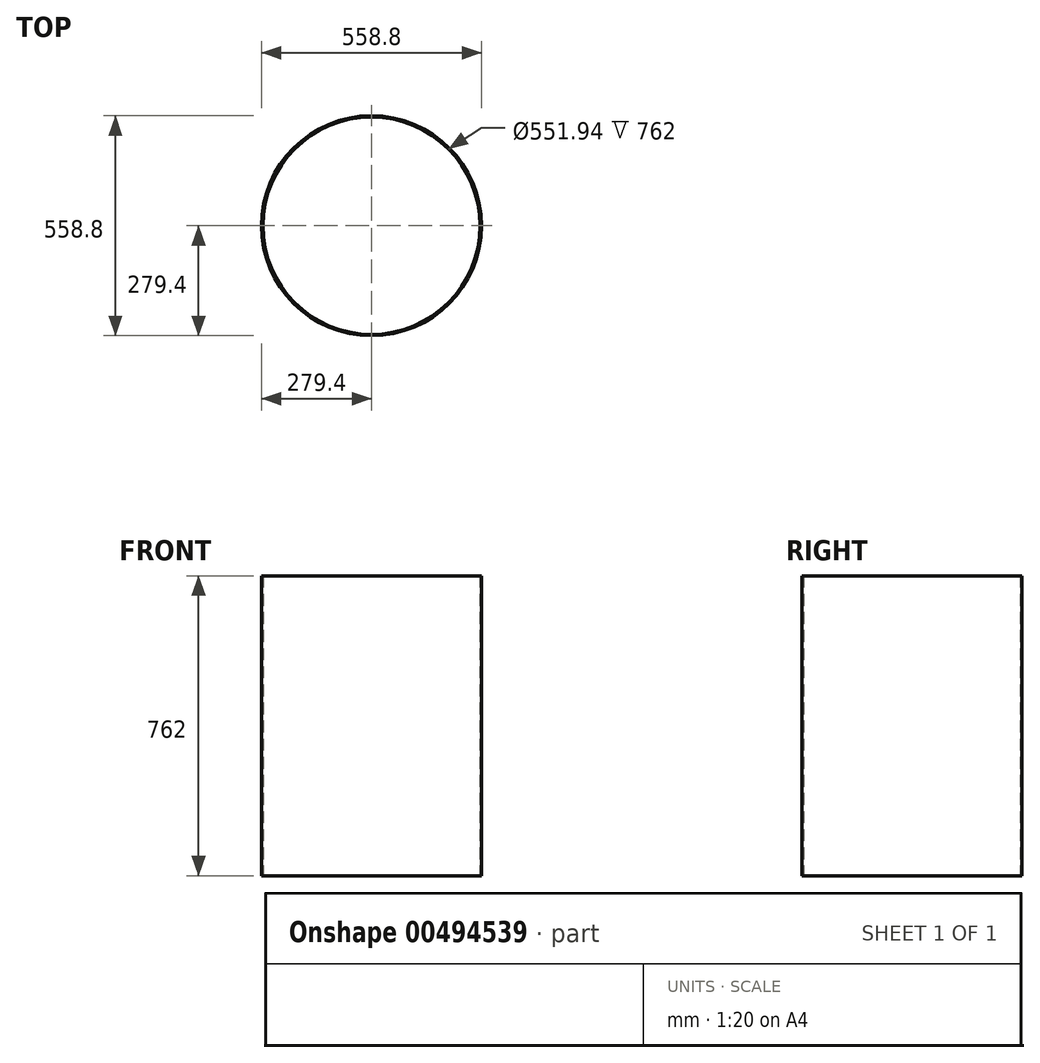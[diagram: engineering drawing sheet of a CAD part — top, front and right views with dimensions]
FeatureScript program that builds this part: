
annotation { "Feature Type Name" : "Feature", "Feature Type Description" : "" }
export const myFeature = defineFeature(function(context is Context, id is Id, definition is map)
    precondition{}
    {
        {
            var Q0;
            Q0=qCreatedBy(makeId("Top.planeOp"),FACE);
            var sketch = newSketch(context, id + "F0", { "sketchPlane" : qUnion([Q0])});
            skCircle(sketch, "E0", {"center": v(0, 0) * mm, "radius": 279.4 * mm});
            skCircle(sketch, "E1", {"center": v(0, 0) * mm, "radius": 275.97 * mm});
            skSolve(sketch);
        }
        {
            var Q0;
            Q0=makeQuery(id+"F0.imprint","IMPRINT",FACE,{"disambiguationData":[TD([[makeQuery(id+"F0.imprint","IMPRINT",EDGE,{"derivedFrom":sQuery(id+"F0.wireOp",EDGE,"E0")}),1.0]])]});
            extrude(context, id + "F1", {"entities" : qUnion([Q0]), "depth" : 762 * mm});
        }
    });
